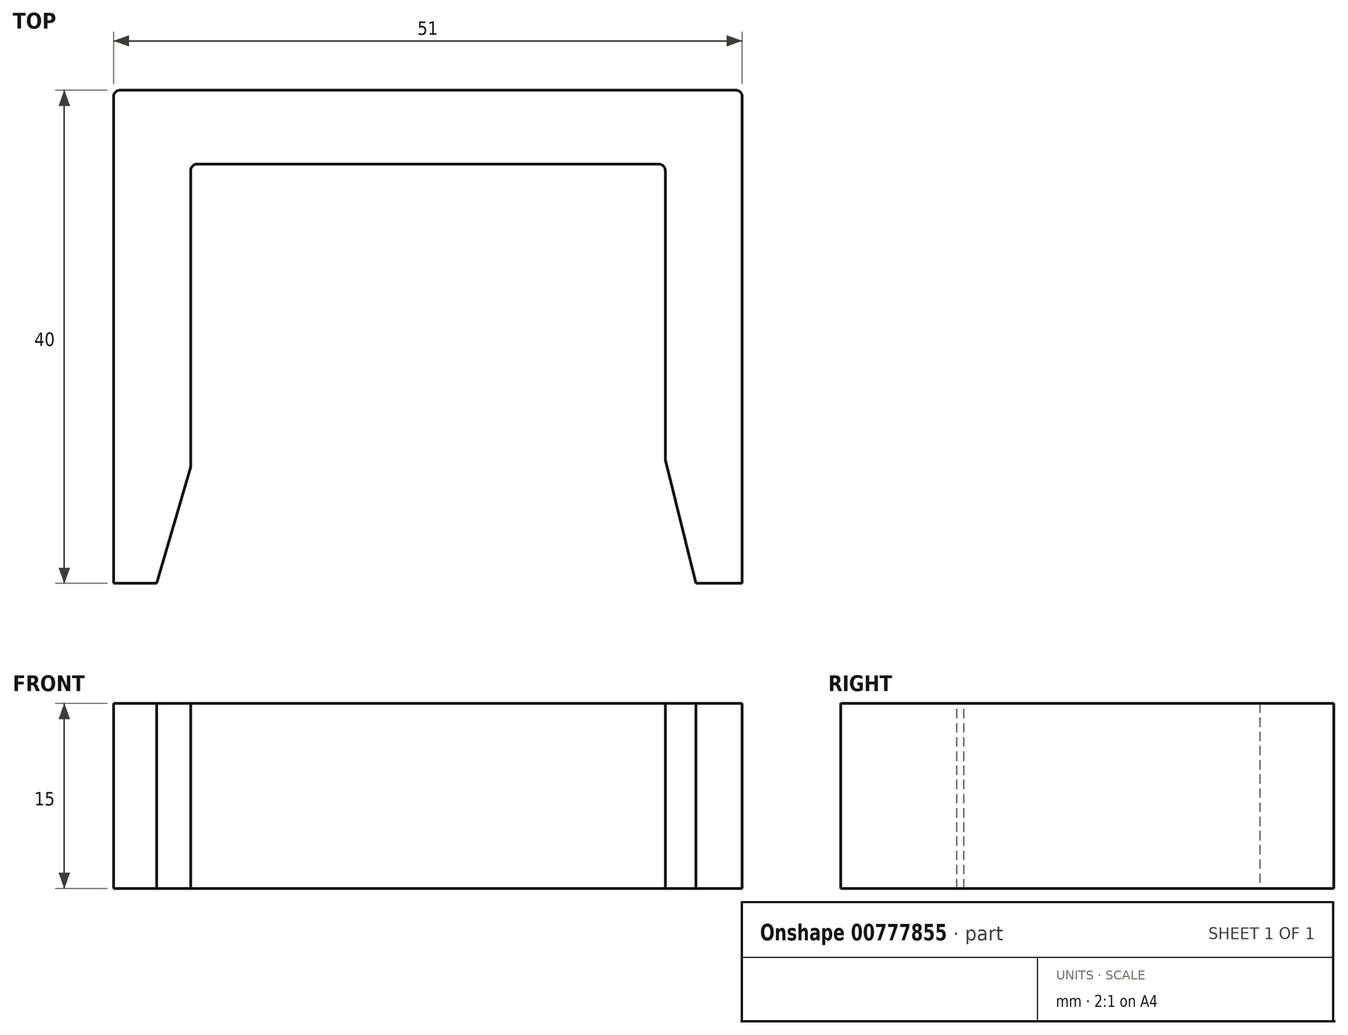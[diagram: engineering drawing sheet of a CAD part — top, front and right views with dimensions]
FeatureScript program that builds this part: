
annotation { "Feature Type Name" : "Feature", "Feature Type Description" : "" }
export const myFeature = defineFeature(function(context is Context, id is Id, definition is map)
    precondition{}
    {
        {
            var Q0;
            Q0=qCreatedBy(makeId("Top.planeOp"),FACE);
            var sketch = newSketch(context, id + "F0", { "sketchPlane" : qUnion([Q0])});
            skLineSegment(sketch, "E0.top", {"start": v(-25.5, 20) * mm, "end": v(25.5, 20) * mm});
            skLineSegment(sketch, "E0.left", {"start": v(-25.5, -20) * mm, "end": v(-25.5, 20) * mm});
            skLineSegment(sketch, "E0.right", {"start": v(25.5, -20) * mm, "end": v(25.5, 20) * mm});
            skPoint(sketch, "E0.middle", {"position": v(0, 0) * mm});
            skLineSegment(sketch, "E1.top", {"start": v(-19.25, 14) * mm, "end": v(19.25, 14) * mm});
            skLineSegment(sketch, "E1.left", {"start": v(-19.25, -14) * mm, "end": v(-19.25, 14) * mm});
            skLineSegment(sketch, "E1.right", {"start": v(19.25, -14) * mm, "end": v(19.25, 14) * mm});
            skLineSegment(sketch, "E2", {"start": v(19.25, -14) * mm, "end": v(19.25, -20) * mm});
            skLineSegment(sketch, "E3", {"start": v(19.25, -20) * mm, "end": v(25.5, -20) * mm});
            skLineSegment(sketch, "E4", {"start": v(-25.5, -20) * mm, "end": v(-19.5, -20) * mm});
            skLineSegment(sketch, "E5", {"start": v(-19.5, -20) * mm, "end": v(-19.25, -14) * mm});
            skSolve(sketch);
        }
        {
            var Q0;
            Q0 = qSketchRegion(id + "F0", true);
            extrude(context, id + "F1", {"entities" : qUnion([Q0]), "depth" : 15 * mm, "offsetDistance" : 25 * mm});
        }
        {
            var Q0;
            Q0=makeQuery(id+"F1.opExtrude","SWEPT_EDGE",EDGE,{"disambiguationData":[OSD([sQuery(id+"F0.wireOp",EDGE,"E1.top"),sQuery(id+"F0.wireOp",EDGE,"E1.left")])]});
            var Q1;
            Q1=makeQuery(id+"F1.opExtrude","SWEPT_EDGE",EDGE,{"disambiguationData":[OSD([sQuery(id+"F0.wireOp",EDGE,"E1.top"),sQuery(id+"F0.wireOp",EDGE,"E1.right")])]});
            var Q2;
            Q2=makeQuery(id+"F1.opExtrude","SWEPT_EDGE",EDGE,{"disambiguationData":[OSD([sQuery(id+"F0.wireOp",EDGE,"E0.top"),sQuery(id+"F0.wireOp",EDGE,"E0.left")])]});
            var Q3;
            Q3=makeQuery(id+"F1.opExtrude","SWEPT_EDGE",EDGE,{"disambiguationData":[OSD([sQuery(id+"F0.wireOp",EDGE,"E0.top"),sQuery(id+"F0.wireOp",EDGE,"E0.right")])]});
            fillet(context, id + "F2", {"entities" : qUnion([Q0, Q1, Q2, Q3]), "radius" : 0.5 * mm, "tangentPropagation" : true, "allowEdgeOverflow" : false});
        }
        {
            var Q0;
            Q0=makeQuery(id+"F1.opExtrude","SWEPT_EDGE",EDGE,{"disambiguationData":[OSD([sQuery(id+"F0.wireOp",EDGE,"E4"),sQuery(id+"F0.wireOp",EDGE,"E5")])]});
            chamfer(context, id + "F3", {"entities" : qUnion([Q0]), "chamferType" : ChamferType.TWO_OFFSETS, "width1" : 10 * mm, "oppositeDirection" : false, "width2" : 2.5 * mm, "tangentPropagation" : true});
        }
        {
            var Q0;
            Q0=makeQuery(id+"F1.opExtrude","SWEPT_EDGE",EDGE,{"disambiguationData":[OSD([sQuery(id+"F0.wireOp",EDGE,"E2"),sQuery(id+"F0.wireOp",EDGE,"E3")])]});
            chamfer(context, id + "F4", {"entities" : qUnion([Q0]), "chamferType" : ChamferType.TWO_OFFSETS, "width1" : 10 * mm, "oppositeDirection" : true, "width2" : 2.5 * mm, "tangentPropagation" : true});
        }
    });
